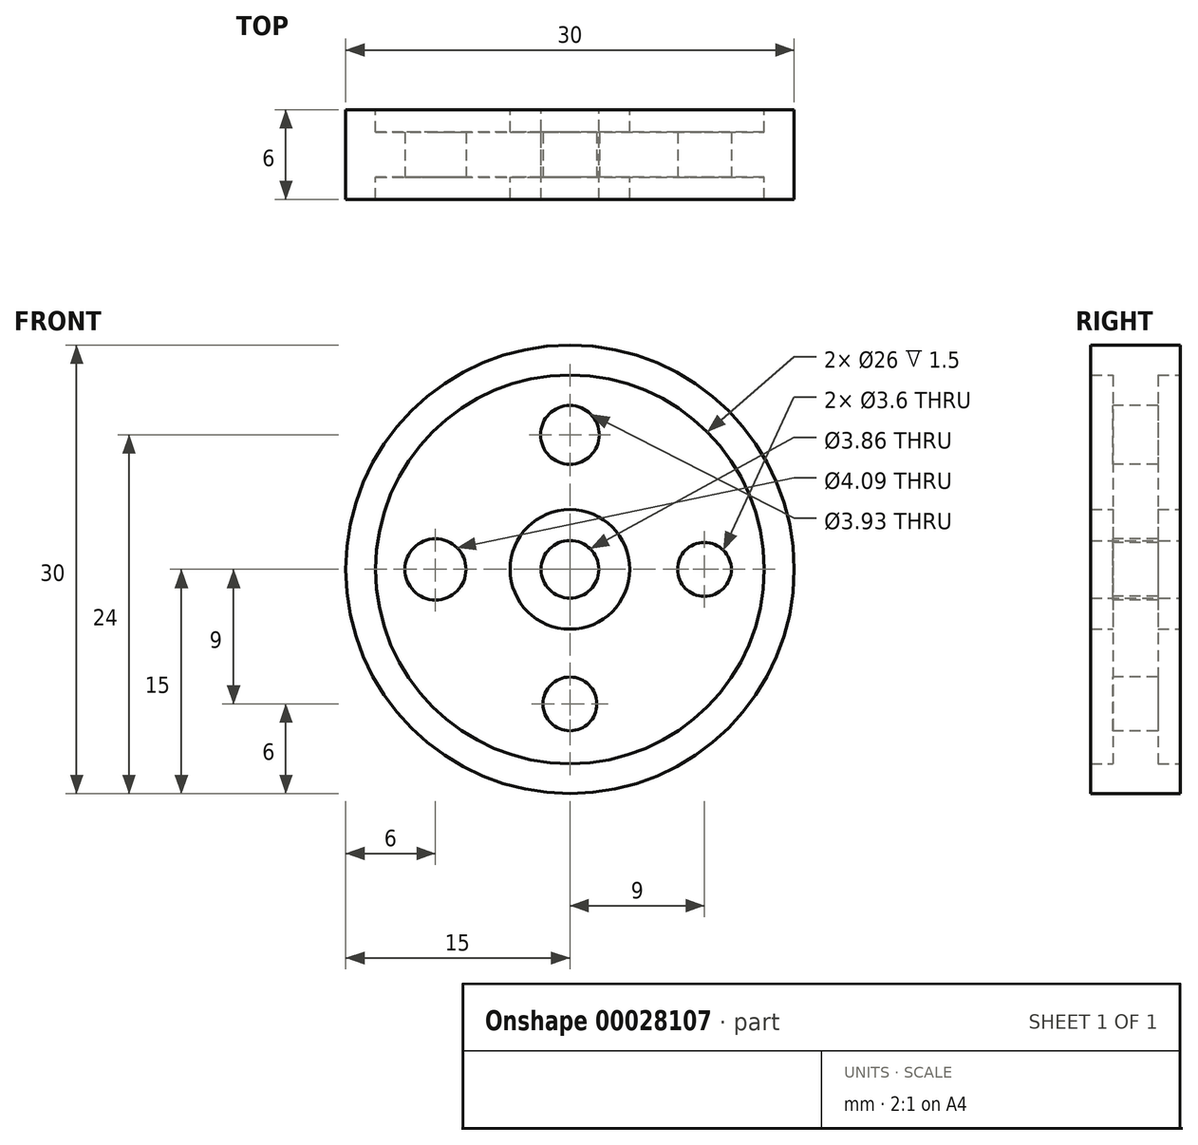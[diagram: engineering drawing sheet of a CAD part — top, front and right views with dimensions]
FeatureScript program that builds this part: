
annotation { "Feature Type Name" : "Feature", "Feature Type Description" : "" }
export const myFeature = defineFeature(function(context is Context, id is Id, definition is map)
    precondition{}
    {
        {
            var Q0;
            Q0=qCreatedBy(makeId("Right.planeOp"),FACE);
            var sketch = newSketch(context, id + "F0", { "sketchPlane" : qUnion([Q0])});
            skLineSegment(sketch, "E0", {"start": v(0, 0) * mm, "end": v(-10.79, 0) * mm, "construction": true});
            skLineSegment(sketch, "E1.bottom", {"start": v(2.86, 1.93) * mm, "end": v(-3.14, 1.93) * mm});
            skLineSegment(sketch, "E1.top", {"start": v(2.86, 4) * mm, "end": v(-3.14, 4) * mm});
            skLineSegment(sketch, "E1.left", {"start": v(2.86, 1.93) * mm, "end": v(2.86, 4) * mm});
            skLineSegment(sketch, "E1.right", {"start": v(-3.14, 1.93) * mm, "end": v(-3.14, 4) * mm});
            skLineSegment(sketch, "E2.bottom", {"start": v(1.36, 4) * mm, "end": v(-1.64, 4) * mm});
            skLineSegment(sketch, "E2.left", {"start": v(1.36, 4) * mm, "end": v(1.36, 13) * mm});
            skLineSegment(sketch, "E2.right", {"start": v(-1.64, 4) * mm, "end": v(-1.64, 13) * mm});
            skLineSegment(sketch, "E3.bottom", {"start": v(2.86, 13) * mm, "end": v(1.36, 13) * mm});
            skLineSegment(sketch, "E3.top", {"start": v(2.86, 15) * mm, "end": v(-3.14, 15) * mm});
            skLineSegment(sketch, "E3.left", {"start": v(2.86, 13) * mm, "end": v(2.86, 15) * mm});
            skLineSegment(sketch, "E3.right", {"start": v(-3.14, 13) * mm, "end": v(-3.14, 15) * mm});
            skLineSegment(sketch, "E4.trimOffspring", {"start": v(-1.64, 13) * mm, "end": v(-3.14, 13) * mm});
            skSolve(sketch);
        }
        {
            var Q0;
            Q0=qSketchRegion(id+"F0",true);
            var Q1;
            Q1=sQuery(id+"F0.wireOp",EDGE,"E0");
            revolve(context, id + "F1", {"entities" : qUnion([Q0]), "axis" : qUnion([Q1]), "revolveType" : RevolveType.FULL});
        }
        {
            var Q0;
            Q0=makeQuery(id+"F1.opRevolve","SWEPT_FACE",FACE,{"disambiguationData":[OSD([sQuery(id+"F0.wireOp",EDGE,"E2.right")])]});
            var sketch = newSketch(context, id + "F2", { "sketchPlane" : qUnion([Q0])});
            skCircle(sketch, "E5", {"center": v(0, 9) * mm, "radius": 1.97 * mm});
            skCircle(sketch, "E6", {"center": v(9, 0) * mm, "radius": 1.8 * mm});
            skCircle(sketch, "E7", {"center": v(0, -9) * mm, "radius": 1.8 * mm});
            skCircle(sketch, "E8", {"center": v(-9, 0) * mm, "radius": 2.04 * mm});
            skSolve(sketch);
        }
        {
            var Q0;
            Q0=qSketchRegion(id+"F2",true);
            extrude(context, id + "F3", {"entities" : qUnion([Q0]), "operationType" : NewBodyOperationType.REMOVE, "endBound" : BoundingType.THROUGH_ALL, "oppositeDirection" : true, "depth" : 25 * mm});
        }
    });
